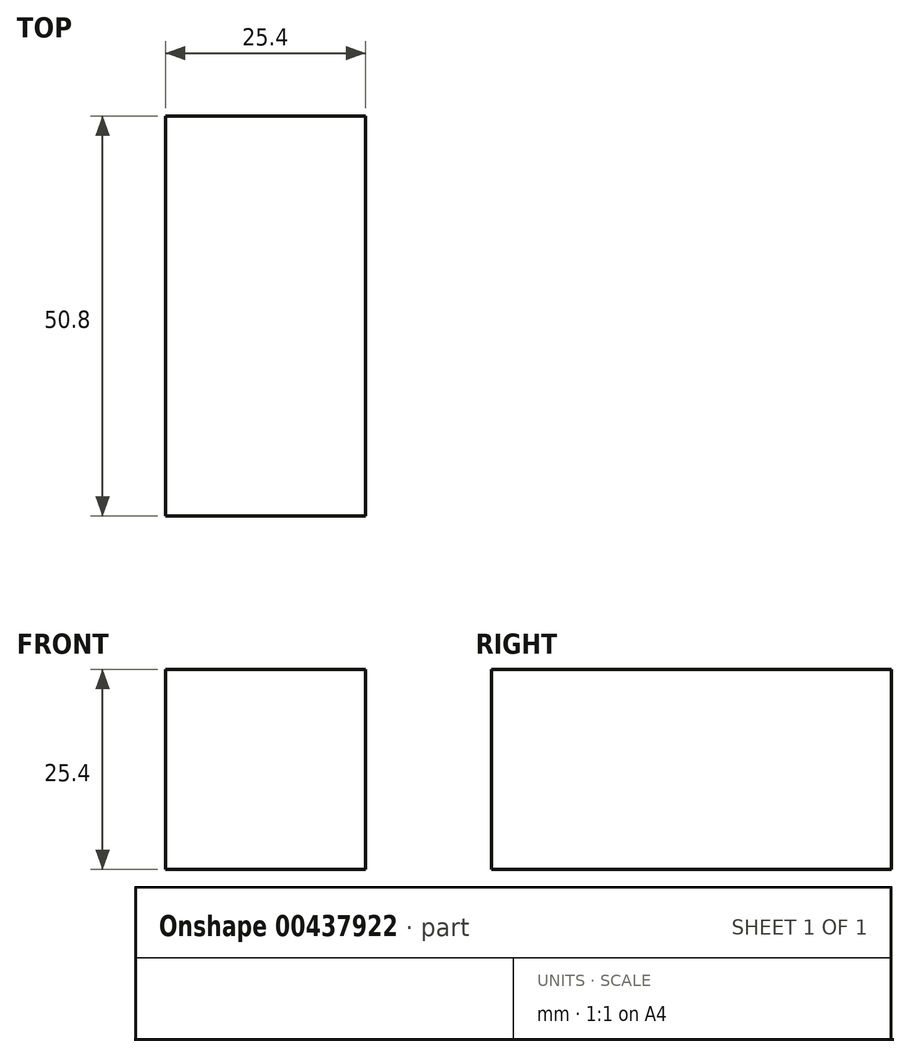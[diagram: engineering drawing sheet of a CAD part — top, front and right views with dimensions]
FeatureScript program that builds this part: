
annotation { "Feature Type Name" : "Feature", "Feature Type Description" : "" }
export const myFeature = defineFeature(function(context is Context, id is Id, definition is map)
    precondition{}
    {
        {
            var Q0;
            Q0=qCreatedBy(makeId("Front.planeOp"),FACE);
            var sketch = newSketch(context, id + "F0", { "sketchPlane" : qUnion([Q0])});
            skLineSegment(sketch, "E0.bottom", {"start": v(-10.5, 9.55) * mm, "end": v(14.9, 9.55) * mm});
            skLineSegment(sketch, "E0.top", {"start": v(-10.5, -15.85) * mm, "end": v(14.9, -15.85) * mm});
            skLineSegment(sketch, "E0.left", {"start": v(-10.5, 9.55) * mm, "end": v(-10.5, -15.85) * mm});
            skLineSegment(sketch, "E0.right", {"start": v(14.9, 9.55) * mm, "end": v(14.9, -15.85) * mm});
            skSolve(sketch);
        }
        {
            var Q0;
            Q0 = qSketchRegion(id + "F0", true);
            extrude(context, id + "F1", {"entities" : qUnion([Q0]), "depth" : 50.8 * mm});
        }
    });
